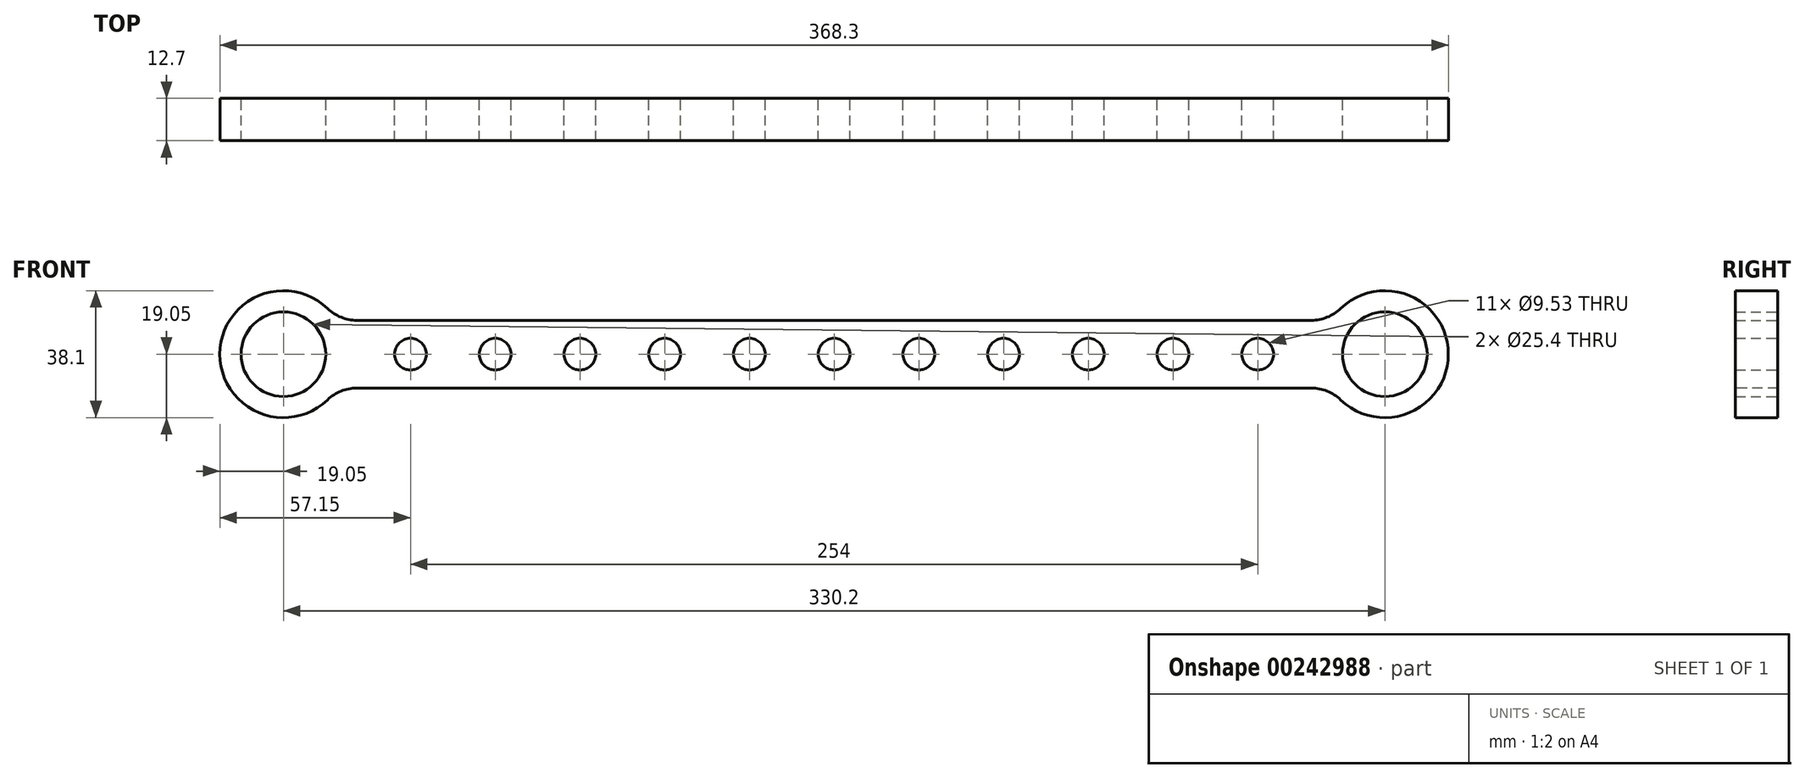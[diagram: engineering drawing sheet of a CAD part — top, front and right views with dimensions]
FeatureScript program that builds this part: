
annotation { "Feature Type Name" : "Feature", "Feature Type Description" : "" }
export const myFeature = defineFeature(function(context is Context, id is Id, definition is map)
    precondition{}
    {
        {
            var Q0;
            Q0=qCreatedBy(makeId("Front.planeOp"),FACE);
            var sketch = newSketch(context, id + "F0", { "sketchPlane" : qUnion([Q0])});
            skArc(sketch, "E0", {"start": v(-16.11, -10.16) * mm, "mid": v(19.05, 0) * mm, "end": v(-16.11, 10.16) * mm});
            skArc(sketch, "E1", {"start": v(-314.09, 10.16) * mm, "mid": v(-349.25, 0) * mm, "end": v(-314.09, -10.16) * mm});
            skLineSegment(sketch, "E2", {"start": v(-314.09, 10.16) * mm, "end": v(-16.11, 10.16) * mm});
            skLineSegment(sketch, "E3", {"start": v(-311.15, 0) * mm, "end": v(-19.05, 0) * mm, "construction": true});
            skLineSegment(sketch, "E4.MirrorCS", {"start": v(-314.09, -10.16) * mm, "end": v(-16.11, -10.16) * mm});
            skCircle(sketch, "E5", {"center": v(-330.2, 0) * mm, "radius": 12.7 * mm});
            skCircle(sketch, "E6", {"center": v(0, 0) * mm, "radius": 12.7 * mm});
            skPoint(sketch, "E7", {"position": v(-292.1, 0) * mm});
            skPoint(sketch, "E8.1.0.0", {"position": v(-266.7, 0) * mm});
            skPoint(sketch, "E8.2.0.0", {"position": v(-241.3, 0) * mm});
            skPoint(sketch, "E8.3.0.0", {"position": v(-215.9, 0) * mm});
            skPoint(sketch, "E8.4.0.0", {"position": v(-190.5, 0) * mm});
            skPoint(sketch, "E8.5.0.0", {"position": v(-165.1, 0) * mm});
            skPoint(sketch, "E8.6.0.0", {"position": v(-139.7, 0) * mm});
            skPoint(sketch, "E8.7.0.0", {"position": v(-114.3, 0) * mm});
            skPoint(sketch, "E8.8.0.0", {"position": v(-88.9, 0) * mm});
            skPoint(sketch, "E8.9.0.0", {"position": v(-63.5, 0) * mm});
            skLineSegment(sketch, "E8.direction1", {"start": v(-292.1, 0) * mm, "end": v(-266.7, 0) * mm, "construction": true});
            skPoint(sketch, "E9.0.10.0", {"position": v(-38.1, 0) * mm});
            skSolve(sketch);
        }
        {
            var Q0;
            Q0 = qSketchRegion(id + "F0", true);
            extrude(context, id + "F1", {"entities" : qUnion([Q0]), "depth" : 12.7 * mm});
        }
        {
            var Q0;
            Q0=sQuery(id+"F0.wireOp",VERTEX,"E7");
            var Q1;
            Q1=sQuery(id+"F0.wireOp",VERTEX,"E8.1.0.0");
            var Q2;
            Q2=sQuery(id+"F0.wireOp",VERTEX,"E8.2.0.0");
            var Q3;
            Q3=sQuery(id+"F0.wireOp",VERTEX,"E8.3.0.0");
            var Q4;
            Q4=sQuery(id+"F0.wireOp",VERTEX,"E8.4.0.0");
            var Q5;
            Q5=sQuery(id+"F0.wireOp",VERTEX,"E8.5.0.0");
            var Q6;
            Q6=sQuery(id+"F0.wireOp",VERTEX,"E8.6.0.0");
            var Q7;
            Q7=sQuery(id+"F0.wireOp",VERTEX,"E8.7.0.0");
            var Q8;
            Q8=sQuery(id+"F0.wireOp",VERTEX,"E8.8.0.0");
            var Q9;
            Q9=sQuery(id+"F0.wireOp",VERTEX,"E8.9.0.0");
            var Q10;
            Q10=sQuery(id+"F0.wireOp",VERTEX,"E9.0.10.0");
            var Q11;
            Q11=makeQuery(id+"F1.opExtrude","SWEPT_BODY",BODY,{"disambiguationData":[OSD([sQuery(id+"F0.wireOp",EDGE,"E0"),sQuery(id+"F0.wireOp",EDGE,"E1"),sQuery(id+"F0.wireOp",EDGE,"E2"),sQuery(id+"F0.wireOp",EDGE,"E4.MirrorCS"),sQuery(id+"F0.wireOp",EDGE,"E5"),sQuery(id+"F0.wireOp",EDGE,"E6")])]});
            hole(context, id + "F2", {"style" : HoleStyle.SIMPLE, "endStyle" : HoleEndStyle.THROUGH, "oppositeDirection" : true, "holeDiameter" : 9.52 * mm, "tappedDepth" : 12.7 * mm, "tapClearance" : 3, "startFromSketch" : true, "locations" : qUnion([Q0, Q1, Q2, Q3, Q4, Q5, Q6, Q7, Q8, Q9, Q10]), "scope" : qUnion([Q11])});
        }
        {
            var Q0;
            Q0=makeQuery(id+"F1.opExtrude","SWEPT_EDGE",EDGE,{"disambiguationData":[OSD([sQuery(id+"F0.wireOp",EDGE,"E1"),sQuery(id+"F0.wireOp",EDGE,"E4.MirrorCS")])]});
            var Q1;
            Q1=makeQuery(id+"F1.opExtrude","SWEPT_EDGE",EDGE,{"disambiguationData":[OSD([sQuery(id+"F0.wireOp",EDGE,"E0"),sQuery(id+"F0.wireOp",EDGE,"E4.MirrorCS")])]});
            var Q2;
            Q2=makeQuery(id+"F1.opExtrude","SWEPT_EDGE",EDGE,{"disambiguationData":[OSD([sQuery(id+"F0.wireOp",EDGE,"E0"),sQuery(id+"F0.wireOp",EDGE,"E2")])]});
            var Q3;
            Q3=makeQuery(id+"F1.opExtrude","SWEPT_EDGE",EDGE,{"disambiguationData":[OSD([sQuery(id+"F0.wireOp",EDGE,"E1"),sQuery(id+"F0.wireOp",EDGE,"E2")])]});
            fillet(context, id + "F3", {"entities" : qUnion([Q0, Q1, Q2, Q3]), "radius" : 12.7 * mm, "tangentPropagation" : true, "allowEdgeOverflow" : false});
        }
    });
